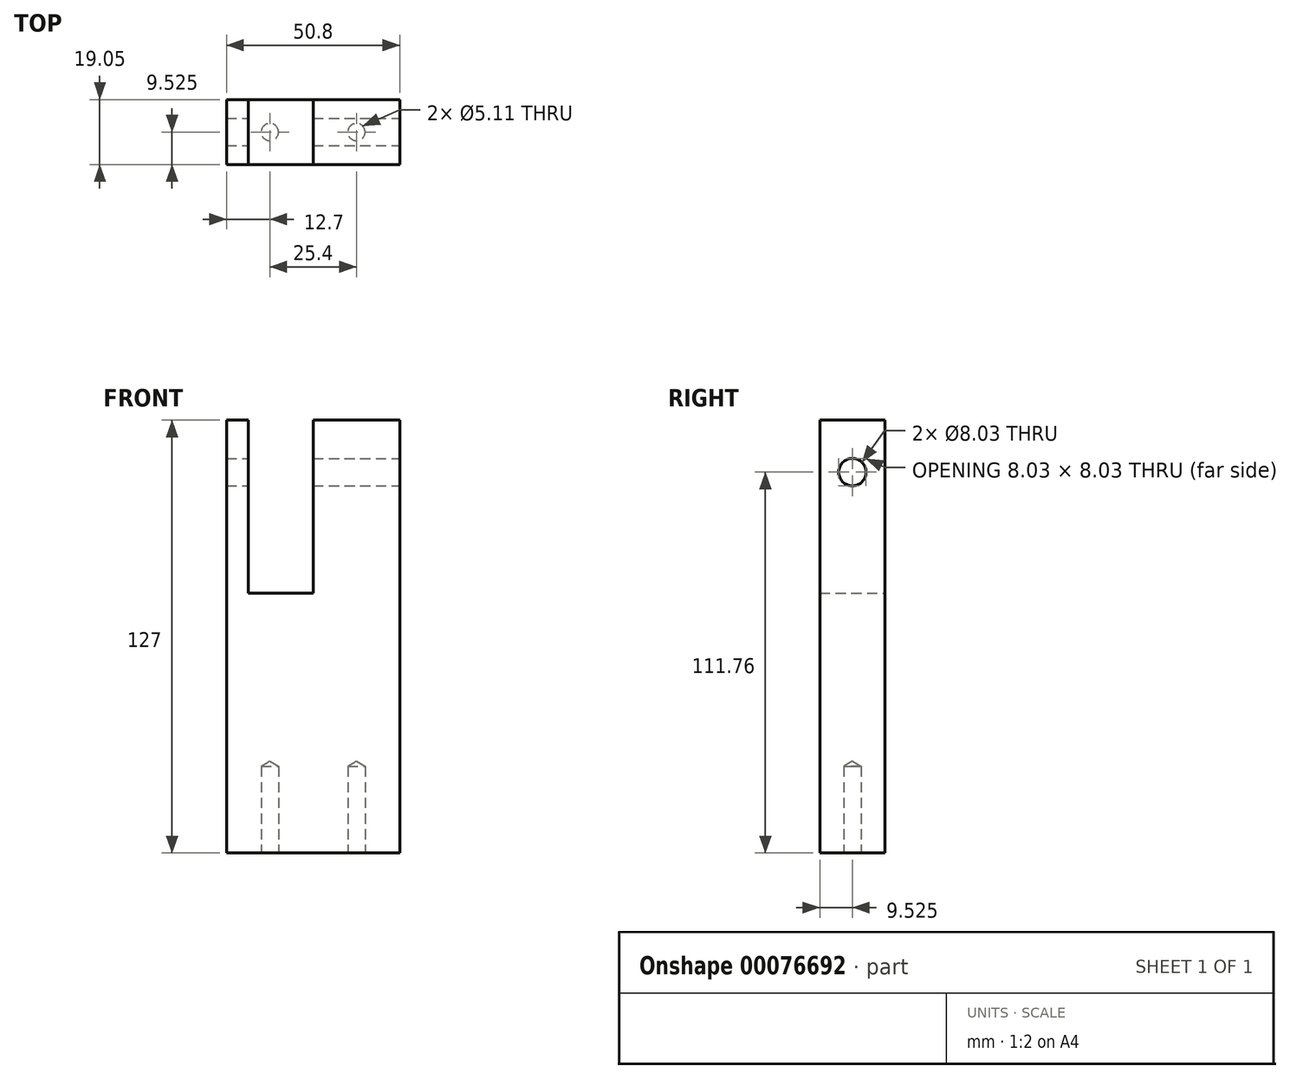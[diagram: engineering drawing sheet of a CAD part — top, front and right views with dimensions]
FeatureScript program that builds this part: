
annotation { "Feature Type Name" : "Feature", "Feature Type Description" : "" }
export const myFeature = defineFeature(function(context is Context, id is Id, definition is map)
    precondition{}
    {
        {
            var Q0;
            Q0=qCreatedBy(makeId("Front.planeOp"),FACE);
            var sketch = newSketch(context, id + "F0", { "sketchPlane" : qUnion([Q0])});
            skLineSegment(sketch, "E0", {"start": v(0, 0) * mm, "end": v(-50.8, 0) * mm});
            skLineSegment(sketch, "E1", {"start": v(-50.8, 0) * mm, "end": v(-50.8, 127) * mm});
            skLineSegment(sketch, "E2", {"start": v(-50.8, 127) * mm, "end": v(-44.45, 127) * mm});
            skLineSegment(sketch, "E3", {"start": v(-44.45, 127) * mm, "end": v(-44.45, 76.2) * mm});
            skLineSegment(sketch, "E4", {"start": v(-44.45, 76.2) * mm, "end": v(-25.4, 76.2) * mm});
            skLineSegment(sketch, "E5", {"start": v(-25.4, 76.2) * mm, "end": v(-25.4, 127) * mm});
            skLineSegment(sketch, "E6", {"start": v(-25.4, 127) * mm, "end": v(0, 127) * mm});
            skLineSegment(sketch, "E7", {"start": v(0, 127) * mm, "end": v(0, 0) * mm});
            skSolve(sketch);
        }
        {
            var Q0;
            Q0=makeQuery(id+"F0.imprint","IMPRINT",FACE,{"disambiguationData":[TD([[makeQuery(id+"F0.imprint","IMPRINT",EDGE,{"derivedFrom":sQuery(id+"F0.wireOp",EDGE,"E0")}),-1.0]])]});
            extrude(context, id + "F1", {"entities" : qUnion([Q0]), "depth" : 19.05 * mm});
        }
        {
            var Q0;
            Q0=makeQuery(id+"F1.opExtrude","SWEPT_FACE",FACE,{"disambiguationData":[OSD([sQuery(id+"F0.wireOp",EDGE,"E7")])]});
            var sketch = newSketch(context, id + "F2", { "sketchPlane" : qUnion([Q0])});
            skLineSegment(sketch, "E8.0", {"start": v(-19.05, 111.76) * mm, "end": v(0, 111.76) * mm, "construction": true});
            skCircle(sketch, "E9", {"center": v(-9.53, 111.76) * mm, "radius": 4.01 * mm, "construction": true});
            skSolve(sketch);
        }
        {
            var Q0;
            Q0=sQuery(id+"F2.wireOp",VERTEX,"E9.center");
            var Q1;
            Q1=makeQuery(id+"F1.opExtrude","SWEPT_BODY",BODY,{"disambiguationData":[OSD([sQuery(id+"F0.wireOp",EDGE,"E0"),sQuery(id+"F0.wireOp",EDGE,"E1"),sQuery(id+"F0.wireOp",EDGE,"E2"),sQuery(id+"F0.wireOp",EDGE,"E3"),sQuery(id+"F0.wireOp",EDGE,"E4"),sQuery(id+"F0.wireOp",EDGE,"E5"),sQuery(id+"F0.wireOp",EDGE,"E6"),sQuery(id+"F0.wireOp",EDGE,"E7")])]});
            hole(context, id + "F3", {"style" : HoleStyle.SIMPLE, "endStyle" : HoleEndStyle.THROUGH, "holeDiameter" : 8.03 * mm, "locations" : qUnion([Q0]), "scope" : qUnion([Q1]), "isTappedThrough" : true});
        }
        {
            var Q0;
            Q0=makeQuery(id+"F1.opExtrude","SWEPT_FACE",FACE,{"disambiguationData":[OSD([sQuery(id+"F0.wireOp",EDGE,"E0")])]});
            var sketch = newSketch(context, id + "F4", { "sketchPlane" : qUnion([Q0])});
            skLineSegment(sketch, "E10.0", {"start": v(-38.1, 19.05) * mm, "end": v(-38.1, 0) * mm, "construction": true});
            skLineSegment(sketch, "E11.0", {"start": v(-12.7, 19.05) * mm, "end": v(-12.7, 0) * mm, "construction": true});
            skCircle(sketch, "E12", {"center": v(-38.1, 9.53) * mm, "radius": 2.55 * mm, "construction": true});
            skCircle(sketch, "E13", {"center": v(-12.7, 9.53) * mm, "radius": 2.55 * mm, "construction": true});
            skSolve(sketch);
        }
        {
            var Q0;
            Q0=sQuery(id+"F4.wireOp",VERTEX,"E12.center");
            var Q1;
            Q1=sQuery(id+"F4.wireOp",VERTEX,"E13.center");
            var Q2;
            Q2=makeQuery(id+"F1.opExtrude","SWEPT_BODY",BODY,{"disambiguationData":[OSD([sQuery(id+"F0.wireOp",EDGE,"E0"),sQuery(id+"F0.wireOp",EDGE,"E1"),sQuery(id+"F0.wireOp",EDGE,"E2"),sQuery(id+"F0.wireOp",EDGE,"E3"),sQuery(id+"F0.wireOp",EDGE,"E4"),sQuery(id+"F0.wireOp",EDGE,"E5"),sQuery(id+"F0.wireOp",EDGE,"E6"),sQuery(id+"F0.wireOp",EDGE,"E7")])]});
            hole(context, id + "F5", {"style" : HoleStyle.SIMPLE, "endStyle" : HoleEndStyle.BLIND, "holeDiameter" : 5.1 * mm, "holeDepth" : 25.4 * mm, "locations" : qUnion([Q0, Q1]), "scope" : qUnion([Q2])});
        }
    });
